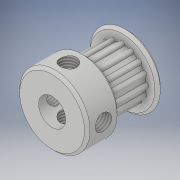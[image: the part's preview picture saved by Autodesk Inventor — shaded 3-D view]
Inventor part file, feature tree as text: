
AUTODESK INVENTOR PART (.ipt)
format: ipt  version: 2019 (Build 230136000, 136)  size: 237,568 bytes
history: native  units: in
note: dims shown in document units (in); Inventor stores cm internally (conversion verified against a paired STEP export)
features: sketch x7, extrude x6, thread x4, pattern_circular x2, chamfer x1
ambient origin geometry x8: Origin, YZ Plane, XZ Plane, XY Plane, X Axis, Y Axis, Z Axis, Center Point
bodies: Solid1 (feature_tree)
feature tree (20):
  extrude  "Extrusion1"  Depth=0.0375in
  extrude  "Extrusion2"  Depth=6.2992in TaperAngle=360.0deg
  pattern_circular  "Circular Pattern1"  [2 undecoded]
  extrude  "Extrusion3"  Depth=0.3937in
  extrude  "Extrusion4"  Depth=0.5118in TaperAngle=0.0deg
  sketch  "Sketch5"  dims[d14=0.5118in]
  extrude  "Extrusion5"  Depth=0.3937in TaperAngle=360.0deg
  pattern_circular  "Circular Pattern2"  [2 undecoded]
  thread  "Thread1"  [1 undecoded]
  thread  "Thread2"  [1 undecoded]
  thread  "Thread3"  [1 undecoded]
  thread  "Thread4"  [1 undecoded]
  extrude  "Extrusion6"  Depth=0.3937in TaperAngle=0.0deg
  chamfer  "Chamfer1"  Distance=0.0197in Angle=45.0deg
  sketch  "Sketch1"  dims[d3=0.2756in d4=0.0in d5=0.0375in]
  sketch  "Sketch2"  dims[d6=0.2756in d7=0.0in d8=6.2992in d9=360.0deg]
  sketch  "Sketch3"  dims[d11=0.5118in]
  sketch  "Sketch4"  dims[d12=0.2362in d13=0.0in]
  sketch  "Sketch6"  dims[d15=0.0394in d16=0.0in]
  sketch  "Sketch7"  dims[d17=0.2362in d18=0.2362in d19=0.1181in d20=0.5118in d21=0.0in d22=1.5748in d23=360.0deg d25=0.3937in d26=0.0in d27=0.3937in d28=0.0in d29=0.3937in d30=0.0in d31=0.3937in d32=0.0in d33=0.1969in d34=0.5512in d35=0.0in d36=0.0197in d37=0.0787in d38=45.0deg]
note: 8 required parameter values undecoded (feature->parameter linkage not recoverable at this tier; creation-order binding heuristic only, values carry confidence <= 0.55)
